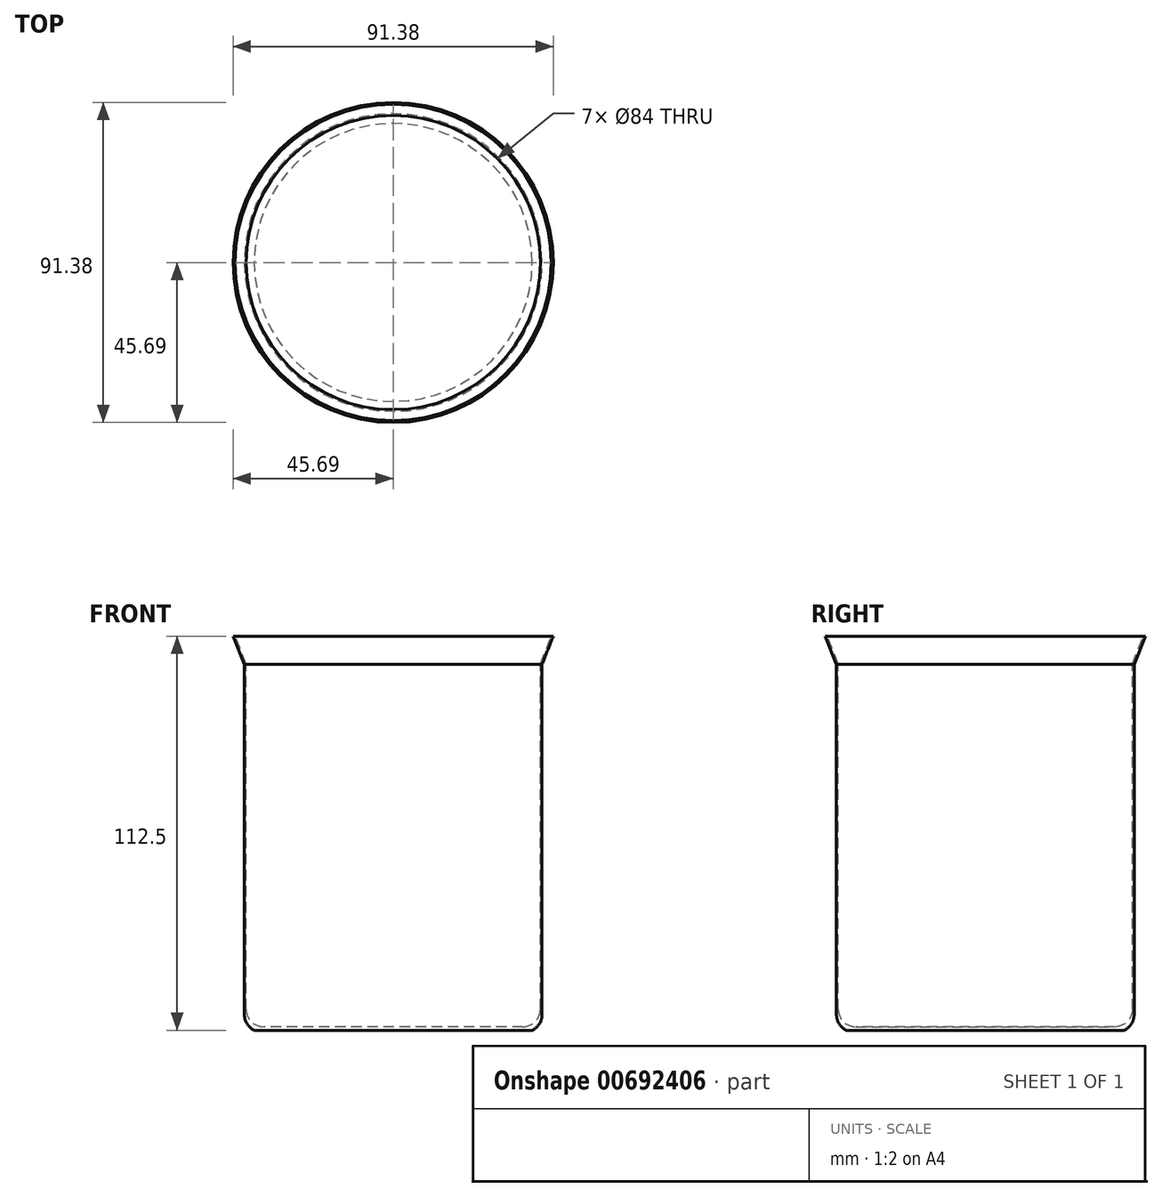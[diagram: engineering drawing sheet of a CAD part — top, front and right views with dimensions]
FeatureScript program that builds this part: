
annotation { "Feature Type Name" : "Feature", "Feature Type Description" : "" }
export const myFeature = defineFeature(function(context is Context, id is Id, definition is map)
    precondition{}
    {
        {
            var Q0;
            Q0=qCreatedBy(makeId("Front.planeOp"),FACE);
            var sketch = newSketch(context, id + "F0", { "sketchPlane" : qUnion([Q0])});
            skLineSegment(sketch, "E0.bottom", {"start": v(-37.5, -56.5) * mm, "end": v(37.5, -56.5) * mm});
            skLineSegment(sketch, "E0.top", {"start": v(-42.5, 56.5) * mm, "end": v(42.5, 56.5) * mm});
            skLineSegment(sketch, "E0.left", {"start": v(-42.5, -51.5) * mm, "end": v(-42.5, 48.5) * mm});
            skLineSegment(sketch, "E0.right", {"start": v(42.5, -51.5) * mm, "end": v(42.5, 56.5) * mm});
            skPoint(sketch, "E0.middle", {"position": v(0, 0) * mm});
            skLineSegment(sketch, "E1.0", {"start": v(-42, -50) * mm, "end": v(-42, 48.6) * mm});
            skLineSegment(sketch, "E1.1", {"start": v(-42, -56) * mm, "end": v(37, -56) * mm});
            skLineSegment(sketch, "E1.2", {"start": v(42, -51) * mm, "end": v(42, 58.5) * mm});
            skLineSegment(sketch, "E2", {"start": v(-42.5, 48.5) * mm, "end": v(-46.5, 58.5) * mm});
            skLineSegment(sketch, "E3.0", {"start": v(-42, 48.6) * mm, "end": v(-45.15, 56.5) * mm});
            skLineSegment(sketch, "E4", {"start": v(-46.5, 58.5) * mm, "end": v(-45.95, 58.5) * mm});
            skPoint(sketch, "E5.orphan", {"position": v(-42, 58.5) * mm});
            skLineSegment(sketch, "E6", {"start": v(0, 56.5) * mm, "end": v(0, 0) * mm, "construction": true});
            skLineSegment(sketch, "E7", {"start": v(0, -56) * mm, "end": v(0, -56.5) * mm});
            skLineSegment(sketch, "E8", {"start": v(-42.5, 56.5) * mm, "end": v(-45.7, 56.5) * mm});
            skLineSegment(sketch, "E9.0", {"start": v(-37, -55) * mm, "end": v(42, -55) * mm});
            skArc(sketch, "E10.0.filletArc", {"start": v(-42, -50) * mm, "mid": v(-40.54, -53.54) * mm, "end": v(-37, -55) * mm});
            skPoint(sketch, "E10.1.visualSharp", {"position": v(-42.5, -56.5) * mm});
            skArc(sketch, "E10.1.filletArc", {"start": v(-42.5, -51.5) * mm, "mid": v(-41.04, -55.04) * mm, "end": v(-37.5, -56.5) * mm});
            skPoint(sketch, "E11.0.visualSharp", {"position": v(42.5, -56.5) * mm});
            skArc(sketch, "E11.0.filletArc", {"start": v(37.5, -56.5) * mm, "mid": v(41.04, -55.04) * mm, "end": v(42.5, -51.5) * mm});
            skPoint(sketch, "E12.0.visualSharp", {"position": v(42, -56) * mm});
            skArc(sketch, "E12.0.filletArc", {"start": v(37, -56) * mm, "mid": v(40.54, -54.54) * mm, "end": v(42, -51) * mm});
            skLineSegment(sketch, "E13", {"start": v(0, -56.5) * mm, "end": v(0, -55) * mm});
            skSolve(sketch);
        }
        {
            var Q0;
            {var subQ3=sQuery(id+"F0.wireOp",EDGE,"E0.left");Q0=makeQuery(id+"F0.imprint","IMPRINT",FACE,{"disambiguationData":[TD([[makeQuery(id+"F0.imprint","IMPRINT",EDGE,{"derivedFrom":subQ3}),-1.0]])]});}
            var Q1;
            Q1=sQuery(id+"F0.wireOp",EDGE,"E6");
            revolve(context, id + "F1", {"entities" : qUnion([Q0]), "axis" : qUnion([Q1]), "revolveType" : RevolveType.FULL});
        }
    });
